# Revit family: Wall_Occupancy_and_Vacancy_Sensor-Lutron-Radio_Powr_Savr-LRF2--
name_source: partatom
category: Lighting Devices
revit_build: Autodesk Revit 2015 (Build: 20160512_0715(x64)
units: mm (PartAtom-declared; Revit-internal decimal feet)

## types (1)
- ERROR_LOAD Type Catalog
    Assembly Code = D5030800
    Current = 14 A
    Default Elevation = 7' - 0"
    Description = Wireless Wall-Mount Sensor
    ENGworks URL = http://www.ENGworks.com
    Field of View = 0.00°
    Flange Depth = 0' - 0 1/4"
    Flange Width = 0' - 0 7/32"
    Frequency and Channel Codes = 431.0 - 437.0 MHz (US; Canada; Mexico; Brazil)
    Label = OS
    Major Motion Coverage = 150.00 SF
    Major Motion Coverage Range = 150' - 0"
    Manufacturer = Lutron Electronics
    Maximum Mounting Height = 8' - 0"
    Maximum Operating Temperature = 104 °F
    Minimum Mounting Height = 6' - 0"
    Minimum Operating Temperature = 32 °F
    Minor Motion Coverage = 0.00 SF
    Minor Motion Coverage Range = 0' - 0"
    Model = LRF2-OHLB-P-WH
    Overall Depth = 0' - 1 11/32"
    Overall Height = 0' - 4 11/32"
    Overall Width = 0' - 1 13/16"
    Product Page URL = http://www.lutron.com
    Range = 30' - 0"
    Sensor Case Radius = 0' - 0 29/32"
    Sensor Cover Arc Depth = 0' - 0 13/32"
    Sensor Cover Depth = 0' - 0 3/4"
    Sensor Cover Height = 0' - 0 29/32"
    Sensor Cover Offset = 0' - 0 1/16"
    Sensor Cover Thickness = 0' - 0 1/8"
    Sensor Cover Vertical Offset = 0' - 0 17/32"
    Sensor Cover Width = 0' - 1 1/4"
    Sensor Material = Plastic - Lutron - White
    Series = Radio Powr Savr
    Standards = cULus® listed; FCC certified; IC certified; COFETEL certified; ANATEL certified; SUTEL certified; Meets CA (U.S.A.) Energy Commission Title 24 requirements
    Thomas Enterprise Solutions URL = http://www.thomasenterprisesolutions.com
    URL = http://www.lutron.com
    Version = 1
    Voltage = 3 V

## geometry (parser evidence)
native form markers: Blend x18, Sweep x2
no freeform markers — native parametric forms only
